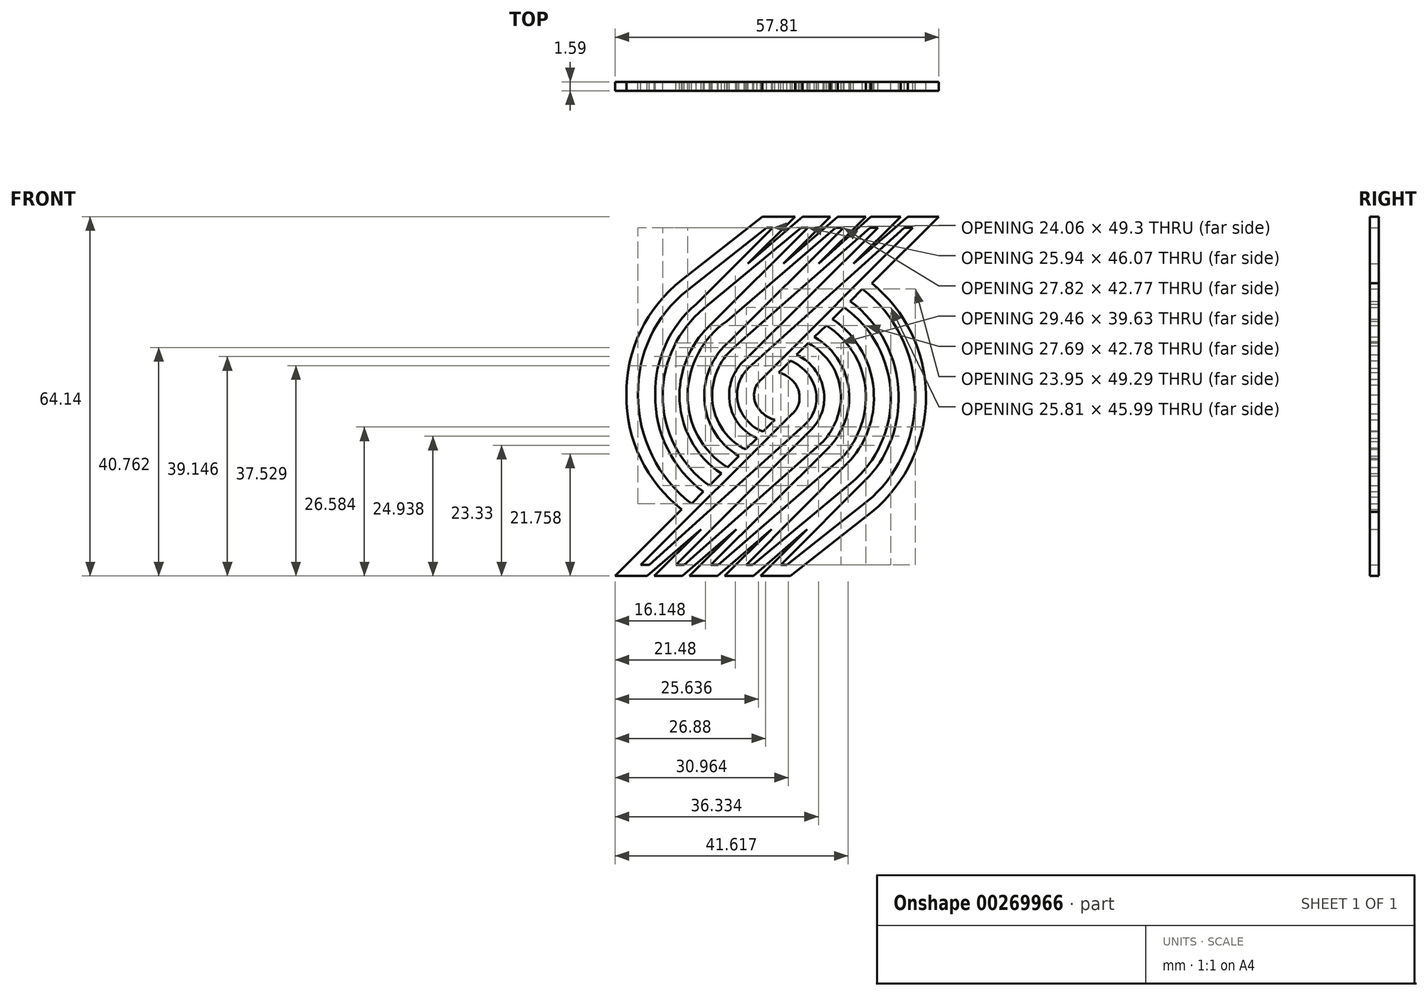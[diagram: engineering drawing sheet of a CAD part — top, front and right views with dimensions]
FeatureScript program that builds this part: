
annotation { "Feature Type Name" : "Feature", "Feature Type Description" : "" }
export const myFeature = defineFeature(function(context is Context, id is Id, definition is map)
    precondition{}
    {
        {
            var Q0;
            Q0=qCreatedBy(makeId("Front.planeOp"),FACE);
            var sketch = newSketch(context, id + "F0", { "sketchPlane" : qUnion([Q0])});
            skLineSegment(sketch, "E0", {"start": v(-3.34, 31.8) * mm, "end": v(2.5, 31.8) * mm});
            skLineSegment(sketch, "E1", {"start": v(2.5, 31.8) * mm, "end": v(-5.9, 23.44) * mm});
            skLineSegment(sketch, "E2", {"start": v(-5.9, 23.44) * mm, "end": v(3.83, 31.8) * mm});
            skLineSegment(sketch, "E3", {"start": v(3.83, 31.8) * mm, "end": v(8.83, 31.8) * mm});
            skLineSegment(sketch, "E4", {"start": v(8.83, 31.8) * mm, "end": v(0.43, 23.44) * mm});
            skLineSegment(sketch, "E5", {"start": v(0.43, 23.44) * mm, "end": v(10.1, 31.8) * mm});
            skLineSegment(sketch, "E6", {"start": v(10.1, 31.8) * mm, "end": v(15.12, 31.8) * mm});
            skLineSegment(sketch, "E7", {"start": v(15.12, 31.8) * mm, "end": v(6.72, 23.44) * mm});
            skLineSegment(sketch, "E8", {"start": v(6.72, 23.44) * mm, "end": v(16.05, 31.8) * mm});
            skLineSegment(sketch, "E9", {"start": v(16.05, 31.8) * mm, "end": v(21.35, 31.8) * mm});
            skLineSegment(sketch, "E10", {"start": v(21.35, 31.8) * mm, "end": v(12.95, 23.44) * mm});
            skLineSegment(sketch, "E11", {"start": v(12.95, 23.44) * mm, "end": v(22.66, 31.8) * mm});
            skLineSegment(sketch, "E12", {"start": v(22.66, 31.8) * mm, "end": v(28.17, 31.8) * mm});
            skLineSegment(sketch, "E13", {"start": v(28.17, 31.8) * mm, "end": v(16.23, 19.92) * mm});
            skLineSegment(sketch, "E14", {"start": v(-29.64, -32.34) * mm, "end": v(-17.75, -20.45) * mm});
            skLineSegment(sketch, "E15", {"start": v(-29.64, -32.34) * mm, "end": v(-23.88, -32.34) * mm});
            skLineSegment(sketch, "E16", {"start": v(-23.88, -32.34) * mm, "end": v(-14.27, -24.03) * mm});
            skLineSegment(sketch, "E17", {"start": v(-14.27, -24.03) * mm, "end": v(-22.64, -32.34) * mm});
            skLineSegment(sketch, "E18", {"start": v(-22.64, -32.34) * mm, "end": v(-17.58, -32.34) * mm});
            skLineSegment(sketch, "E19", {"start": v(-17.58, -32.34) * mm, "end": v(-7.98, -24.03) * mm});
            skLineSegment(sketch, "E20", {"start": v(-7.98, -24.03) * mm, "end": v(-16.35, -32.34) * mm});
            skLineSegment(sketch, "E21", {"start": v(-16.35, -32.34) * mm, "end": v(-11.3, -32.34) * mm});
            skLineSegment(sketch, "E22", {"start": v(-11.3, -32.34) * mm, "end": v(-1.66, -24) * mm});
            skLineSegment(sketch, "E23", {"start": v(-1.66, -24) * mm, "end": v(-10.06, -32.34) * mm});
            skLineSegment(sketch, "E24", {"start": v(-10.06, -32.34) * mm, "end": v(-4.9, -32.34) * mm});
            skLineSegment(sketch, "E25", {"start": v(-4.9, -32.34) * mm, "end": v(4.7, -24.03) * mm});
            skLineSegment(sketch, "E26", {"start": v(4.7, -24.03) * mm, "end": v(-3.66, -32.34) * mm});
            skLineSegment(sketch, "E27", {"start": v(-3.66, -32.34) * mm, "end": v(1.67, -32.34) * mm});
            skArc(sketch, "E28", {"start": v(-27.6, 0) * mm, "mid": v(-25.07, -11.38) * mm, "end": v(-17.75, -20.45) * mm});
            skArc(sketch, "E29", {"start": v(-17.75, 20.47) * mm, "mid": v(-25.07, 11.39) * mm, "end": v(-27.6, 0) * mm});
            skArc(sketch, "E30", {"start": v(25.88, 0) * mm, "mid": v(23.25, 11.03) * mm, "end": v(16.23, 19.92) * mm});
            skArc(sketch, "E31", {"start": v(16.23, -20.93) * mm, "mid": v(23.43, -11.56) * mm, "end": v(25.88, 0) * mm});
            skLineSegment(sketch, "E32", {"start": v(1.67, -32.34) * mm, "end": v(16.23, -20.93) * mm});
            skLineSegment(sketch, "E33", {"start": v(-17.75, 20.47) * mm, "end": v(-3.34, 31.8) * mm});
            skLineSegment(sketch, "E34", {"start": v(-2.54, 29.84) * mm, "end": v(-1.46, 29.84) * mm});
            skLineSegment(sketch, "E35", {"start": v(-2.54, 29.84) * mm, "end": v(-16.76, 18.6) * mm});
            skArc(sketch, "E36", {"start": v(-16.76, 18.6) * mm, "mid": v(-23.33, 10.33) * mm, "end": v(-25.52, 0) * mm});
            skArc(sketch, "E37", {"start": v(-25.52, 0) * mm, "mid": v(-23.02, -10.85) * mm, "end": v(-15.98, -19.46) * mm});
            skLineSegment(sketch, "E38", {"start": v(-15.98, -19.46) * mm, "end": v(-13.84, -17.3) * mm});
            skArc(sketch, "E39", {"start": v(-22.45, 0) * mm, "mid": v(-20.24, -9.7) * mm, "end": v(-13.84, -17.3) * mm});
            skLineSegment(sketch, "E40", {"start": v(-1.46, 29.84) * mm, "end": v(-15.17, 16.2) * mm});
            skArc(sketch, "E41", {"start": v(-15.17, 16.2) * mm, "mid": v(-20.63, 8.91) * mm, "end": v(-22.45, 0) * mm});
            skLineSegment(sketch, "E42", {"start": v(3.62, 29.84) * mm, "end": v(4.8, 29.84) * mm});
            skLineSegment(sketch, "E43", {"start": v(4.8, 29.84) * mm, "end": v(-13, 12.1) * mm});
            skLineSegment(sketch, "E44", {"start": v(3.62, 29.84) * mm, "end": v(-13.79, 15.4) * mm});
            skArc(sketch, "E45", {"start": v(-13.79, 15.4) * mm, "mid": v(-19.15, 8.5) * mm, "end": v(-21.13, 0) * mm});
            skArc(sketch, "E46", {"start": v(-13, 12.1) * mm, "mid": v(-16.75, 6.55) * mm, "end": v(-18.12, 0) * mm});
            skArc(sketch, "E47", {"start": v(-21.13, 0) * mm, "mid": v(-18.93, -9.14) * mm, "end": v(-12.77, -16.23) * mm});
            skArc(sketch, "E48", {"start": v(-18.12, 0) * mm, "mid": v(-16.17, -7.99) * mm, "end": v(-10.65, -14.08) * mm});
            skLineSegment(sketch, "E49", {"start": v(-12.77, -16.23) * mm, "end": v(-10.65, -14.08) * mm});
            skLineSegment(sketch, "E50", {"start": v(9.77, 29.8) * mm, "end": v(11.15, 29.8) * mm});
            skLineSegment(sketch, "E51", {"start": v(11.15, 29.8) * mm, "end": v(-9.24, 9.5) * mm});
            skLineSegment(sketch, "E52", {"start": v(9.77, 29.8) * mm, "end": v(-9.7, 13.1) * mm});
            skArc(sketch, "E53", {"start": v(-9.7, 13.1) * mm, "mid": v(-14.77, 7.4) * mm, "end": v(-16.67, 0) * mm});
            skArc(sketch, "E54", {"start": v(-9.24, 9.5) * mm, "mid": v(-12.5, 5.24) * mm, "end": v(-13.68, 0) * mm});
            skArc(sketch, "E55", {"start": v(-16.67, 0) * mm, "mid": v(-14.8, -7.4) * mm, "end": v(-9.55, -12.97) * mm});
            skArc(sketch, "E56", {"start": v(-13.68, 0) * mm, "mid": v(-12.08, -6.31) * mm, "end": v(-7.48, -10.92) * mm});
            skLineSegment(sketch, "E57", {"start": v(-9.55, -12.97) * mm, "end": v(-7.48, -10.92) * mm});
            skLineSegment(sketch, "E58", {"start": v(15.88, 29.83) * mm, "end": v(17.3, 29.83) * mm});
            skLineSegment(sketch, "E59", {"start": v(15.88, 29.83) * mm, "end": v(-8.07, 8.72) * mm});
            skArc(sketch, "E60", {"start": v(-8.07, 8.72) * mm, "mid": v(-11.16, 4.84) * mm, "end": v(-12.27, 0) * mm});
            skArc(sketch, "E61", {"start": v(-12.27, 0) * mm, "mid": v(-10.72, -5.75) * mm, "end": v(-6.32, -9.76) * mm});
            skLineSegment(sketch, "E62", {"start": v(-6.32, -9.76) * mm, "end": v(-4.3, -7.75) * mm});
            skArc(sketch, "E63", {"start": v(-9.25, 0) * mm, "mid": v(-7.95, -4.63) * mm, "end": v(-4.3, -7.75) * mm});
            skArc(sketch, "E64", {"start": v(-6.56, 6.1) * mm, "mid": v(-8.55, 3.33) * mm, "end": v(-9.25, 0) * mm});
            skLineSegment(sketch, "E65", {"start": v(-6.56, 6.1) * mm, "end": v(17.3, 29.83) * mm});
            skLineSegment(sketch, "E66", {"start": v(22, 29.83) * mm, "end": v(23.54, 29.83) * mm});
            skArc(sketch, "E67", {"start": v(-3.44, 2.78) * mm, "mid": v(-4.74, 0.63) * mm, "end": v(-4.4, -1.87) * mm});
            skArc(sketch, "E68", {"start": v(-4.4, -1.87) * mm, "mid": v(-3.02, -3.52) * mm, "end": v(-1.1, -4.48) * mm});
            skLineSegment(sketch, "E69", {"start": v(-1.1, -4.48) * mm, "end": v(-3.2, -6.58) * mm});
            skArc(sketch, "E70", {"start": v(-7.86, 0) * mm, "mid": v(-6.53, -4) * mm, "end": v(-3.2, -6.58) * mm});
            skArc(sketch, "E71", {"start": v(-5.84, 4.72) * mm, "mid": v(-7.34, 2.57) * mm, "end": v(-7.86, 0) * mm});
            skLineSegment(sketch, "E72", {"start": v(22, 29.83) * mm, "end": v(-5.84, 4.72) * mm});
            skLineSegment(sketch, "E73", {"start": v(-3.44, 2.78) * mm, "end": v(23.54, 29.83) * mm});
            skLineSegment(sketch, "E74", {"start": v(-0.43, 3.98) * mm, "end": v(1.66, 6.06) * mm});
            skLineSegment(sketch, "E75", {"start": v(2.78, 7.16) * mm, "end": v(4.85, 9.23) * mm});
            skArc(sketch, "E76", {"start": v(2.7, 1.77) * mm, "mid": v(1.34, 3.16) * mm, "end": v(-0.43, 3.98) * mm});
            skArc(sketch, "E77", {"start": v(3.16, -1.64) * mm, "mid": v(3.27, 0.1) * mm, "end": v(2.7, 1.77) * mm});
            skArc(sketch, "E78", {"start": v(2, -3.38) * mm, "mid": v(2.72, -2.6) * mm, "end": v(3.16, -1.64) * mm});
            skLineSegment(sketch, "E79", {"start": v(2, -3.38) * mm, "end": v(-25.04, -30.4) * mm});
            skLineSegment(sketch, "E80", {"start": v(-25.04, -30.4) * mm, "end": v(-23.5, -30.4) * mm});
            skLineSegment(sketch, "E81", {"start": v(-23.5, -30.4) * mm, "end": v(4.13, -5.46) * mm});
            skArc(sketch, "E82", {"start": v(4.13, -5.46) * mm, "mid": v(5.87, -2.98) * mm, "end": v(6.35, 0) * mm});
            skArc(sketch, "E83", {"start": v(6.35, 0) * mm, "mid": v(4.85, 3.68) * mm, "end": v(1.66, 6.06) * mm});
            skArc(sketch, "E84", {"start": v(7.72, 0) * mm, "mid": v(6.23, 4.26) * mm, "end": v(2.78, 7.16) * mm});
            skArc(sketch, "E85", {"start": v(5.16, -6.44) * mm, "mid": v(7.16, -3.5) * mm, "end": v(7.72, 0) * mm});
            skLineSegment(sketch, "E86", {"start": v(5.16, -6.44) * mm, "end": v(-18.74, -30.4) * mm});
            skLineSegment(sketch, "E87", {"start": v(-18.74, -30.4) * mm, "end": v(-17.31, -30.4) * mm});
            skLineSegment(sketch, "E88", {"start": v(-17.31, -30.4) * mm, "end": v(7.55, -8.31) * mm});
            skArc(sketch, "E89", {"start": v(7.55, -8.31) * mm, "mid": v(9.92, -4.45) * mm, "end": v(10.73, 0) * mm});
            skArc(sketch, "E90", {"start": v(10.73, 0) * mm, "mid": v(8.99, 5.38) * mm, "end": v(4.85, 9.23) * mm});
            skArc(sketch, "E91", {"start": v(12.2, 0) * mm, "mid": v(10.42, 5.96) * mm, "end": v(5.98, 10.31) * mm});
            skArc(sketch, "E92", {"start": v(8.5, -9.45) * mm, "mid": v(11.3, -5.1) * mm, "end": v(12.2, 0) * mm});
            skLineSegment(sketch, "E93", {"start": v(8.5, -9.45) * mm, "end": v(-12.52, -30.4) * mm});
            skLineSegment(sketch, "E94", {"start": v(-12.52, -30.4) * mm, "end": v(-11.22, -30.4) * mm});
            skLineSegment(sketch, "E95", {"start": v(-11.22, -30.4) * mm, "end": v(10.8, -11.36) * mm});
            skArc(sketch, "E96", {"start": v(10.8, -11.36) * mm, "mid": v(14.08, -6.1) * mm, "end": v(15.17, 0) * mm});
            skArc(sketch, "E97", {"start": v(15.17, 0) * mm, "mid": v(13.19, 7.08) * mm, "end": v(8.09, 12.38) * mm});
            skLineSegment(sketch, "E98", {"start": v(5.98, 10.31) * mm, "end": v(8.09, 12.38) * mm});
            skLineSegment(sketch, "E99", {"start": v(-6.2, -30.4) * mm, "end": v(-5.04, -30.4) * mm});
            skLineSegment(sketch, "E100", {"start": v(-5.04, -30.4) * mm, "end": v(12.44, -15.85) * mm});
            skLineSegment(sketch, "E101", {"start": v(-6.2, -30.4) * mm, "end": v(12.48, -11.59) * mm});
            skArc(sketch, "E102", {"start": v(12.48, -11.59) * mm, "mid": v(15.63, -6.18) * mm, "end": v(16.58, 0) * mm});
            skArc(sketch, "E103", {"start": v(12.44, -15.85) * mm, "mid": v(17.84, -8.75) * mm, "end": v(19.6, 0) * mm});
            skArc(sketch, "E104", {"start": v(16.58, 0) * mm, "mid": v(14.51, 7.65) * mm, "end": v(9.19, 13.52) * mm});
            skArc(sketch, "E105", {"start": v(19.6, 0) * mm, "mid": v(17.26, 8.78) * mm, "end": v(11.27, 15.6) * mm});
            skLineSegment(sketch, "E106", {"start": v(9.19, 13.52) * mm, "end": v(11.27, 15.6) * mm});
            skLineSegment(sketch, "E107", {"start": v(12.34, 16.7) * mm, "end": v(14.5, 18.89) * mm});
            skArc(sketch, "E108", {"start": v(20.98, 0) * mm, "mid": v(18.63, 9.37) * mm, "end": v(12.34, 16.7) * mm});
            skArc(sketch, "E109", {"start": v(23.95, 0) * mm, "mid": v(21.38, 10.52) * mm, "end": v(14.5, 18.89) * mm});
            skArc(sketch, "E110", {"start": v(15.8, -14.52) * mm, "mid": v(19.78, -7.76) * mm, "end": v(20.98, 0) * mm});
            skArc(sketch, "E111", {"start": v(16.37, -18.23) * mm, "mid": v(22.1, -9.93) * mm, "end": v(23.95, 0) * mm});
            skLineSegment(sketch, "E112", {"start": v(15.8, -14.52) * mm, "end": v(0, -30.4) * mm});
            skLineSegment(sketch, "E113", {"start": v(0, -30.4) * mm, "end": v(1.05, -30.4) * mm});
            skLineSegment(sketch, "E114", {"start": v(1.05, -30.4) * mm, "end": v(16.37, -18.23) * mm});
            skSolve(sketch);
        }
        {
            var Q0;
            Q0=makeQuery(id+"F0.imprint","IMPRINT",FACE,{"disambiguationData":[TD([[makeQuery(id+"F0.imprint","IMPRINT",EDGE,{"derivedFrom":sQuery(id+"F0.wireOp",EDGE,"E0")}),-1.0]])]});
            extrude(context, id + "F1", {"entities" : qUnion([Q0]), "depth" : 1.59 * mm});
        }
    });
